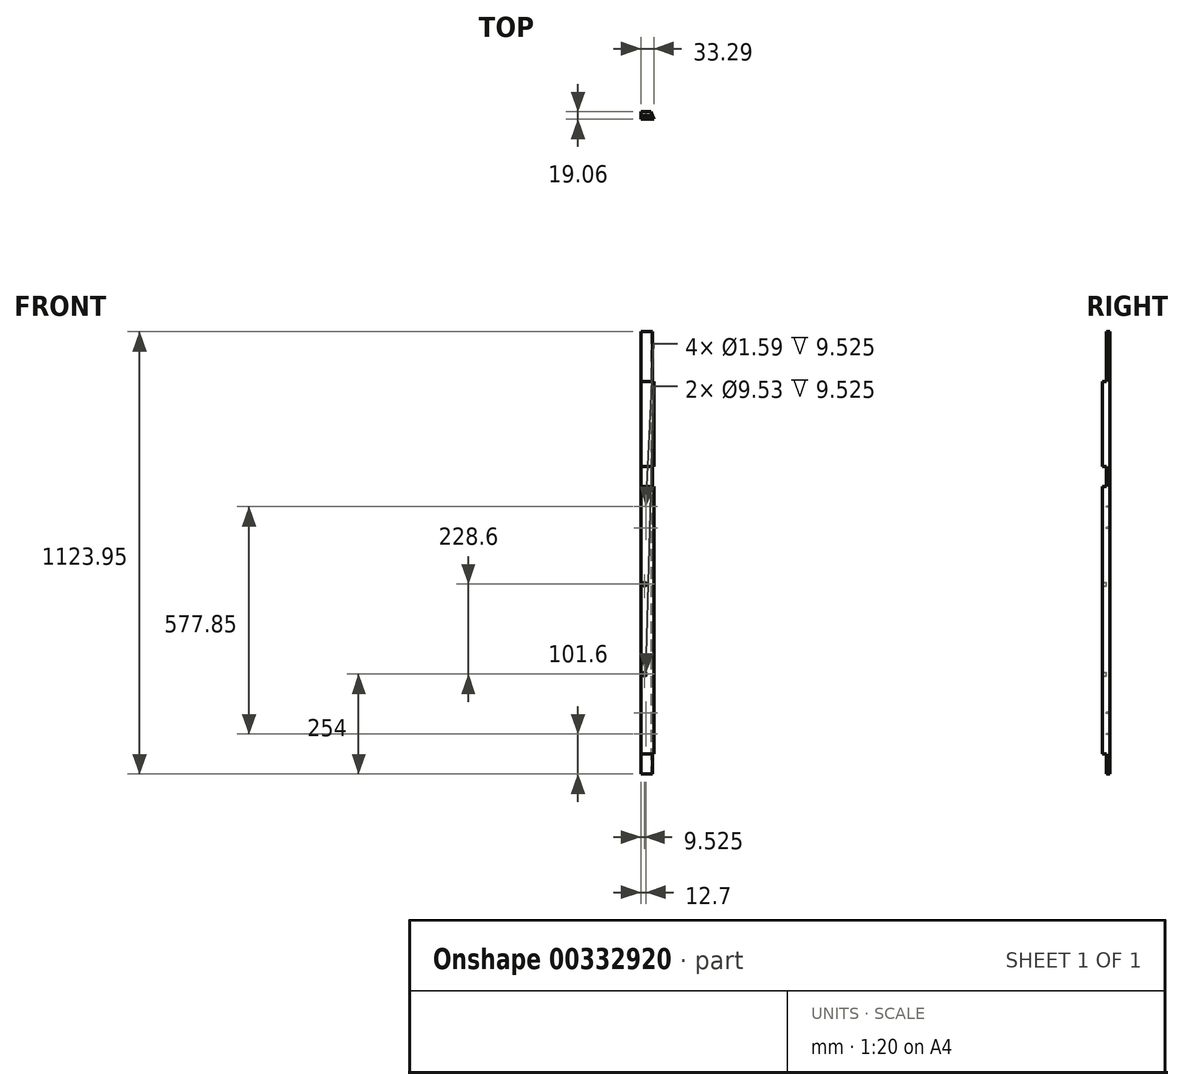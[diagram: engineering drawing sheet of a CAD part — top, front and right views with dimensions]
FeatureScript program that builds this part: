
annotation { "Feature Type Name" : "Feature", "Feature Type Description" : "" }
export const myFeature = defineFeature(function(context is Context, id is Id, definition is map)
    precondition{}
    {
        {
            var Q0;
            Q0=qCreatedBy(makeId("Top.planeOp"),FACE);
            var sketch = newSketch(context, id + "F0", { "sketchPlane" : qUnion([Q0])});
            skLineSegment(sketch, "E0.bottom", {"start": v(0, 9.53) * mm, "end": v(-25.4, 9.53) * mm});
            skLineSegment(sketch, "E0.top", {"start": v(7.9, -9.53) * mm, "end": v(-25.4, -9.53) * mm});
            skLineSegment(sketch, "E0.right", {"start": v(-25.4, 9.53) * mm, "end": v(-25.4, -9.53) * mm});
            skPoint(sketch, "E0.middle", {"position": v(0, 0) * mm});
            skLineSegment(sketch, "E1", {"start": v(0, 9.53) * mm, "end": v(7.9, -9.53) * mm});
            skPoint(sketch, "E0.left.end.orphan", {"position": v(25.4, -9.52) * mm});
            skPoint(sketch, "E2.orphan", {"position": v(25.4, 9.53) * mm});
            skSolve(sketch);
        }
        {
            var Q0;
            Q0=makeQuery(id+"F0.imprint","IMPRINT",FACE,{"disambiguationData":[TD([[makeQuery(id+"F0.imprint","IMPRINT",EDGE,{"derivedFrom":sQuery(id+"F0.wireOp",EDGE,"E0.bottom")}),1.0]])]});
            extrude(context, id + "F1", {"entities" : qUnion([Q0]), "depth" : 1123.95 * mm});
        }
        {
            var Q0;
            Q0=qCreatedBy(makeId("Front.planeOp"),FACE);
            var sketch = newSketch(context, id + "F2", { "sketchPlane" : qUnion([Q0])});
            skLineSegment(sketch, "E3.bottom", {"start": v(-38.77, 0) * mm, "end": v(83.66, 0) * mm});
            skLineSegment(sketch, "E3.top", {"start": v(-38.77, 50.8) * mm, "end": v(83.66, 50.8) * mm});
            skLineSegment(sketch, "E3.left", {"start": v(-38.77, 0) * mm, "end": v(-38.77, 50.8) * mm});
            skLineSegment(sketch, "E3.right", {"start": v(83.66, 0) * mm, "end": v(83.66, 50.8) * mm});
            skLineSegment(sketch, "E4.bottom", {"start": v(-44.21, 730.25) * mm, "end": v(49.65, 730.25) * mm});
            skLineSegment(sketch, "E4.top", {"start": v(-44.21, 781.05) * mm, "end": v(49.65, 781.05) * mm});
            skLineSegment(sketch, "E4.left", {"start": v(-44.21, 730.25) * mm, "end": v(-44.21, 781.05) * mm});
            skLineSegment(sketch, "E4.right", {"start": v(49.65, 730.25) * mm, "end": v(49.65, 781.05) * mm});
            skLineSegment(sketch, "E5.bottom", {"start": v(-210.36, 996.95) * mm, "end": v(132.8, 996.95) * mm});
            skLineSegment(sketch, "E5.top", {"start": v(-210.36, 1123.95) * mm, "end": v(132.8, 1123.95) * mm});
            skLineSegment(sketch, "E5.left", {"start": v(-210.36, 996.95) * mm, "end": v(-210.36, 1123.95) * mm});
            skLineSegment(sketch, "E5.right", {"start": v(132.8, 996.95) * mm, "end": v(132.8, 1123.95) * mm});
            skSolve(sketch);
        }
        {
            var Q0;
            Q0=qSketchRegion(id+"F2",true);
            extrude(context, id + "F3", {"entities" : qUnion([Q0]), "operationType" : NewBodyOperationType.REMOVE, "depth" : 25.4 * mm});
        }
        {
            var Q0;
            Q0=qCreatedBy(makeId("Front.planeOp"),FACE);
            var sketch = newSketch(context, id + "F4", { "sketchPlane" : qUnion([Q0])});
            skCircle(sketch, "E6", {"center": v(12.7, 101.6) * mm, "radius": 0.8 * mm});
            skCircle(sketch, "E7", {"center": v(12.7, 155.58) * mm, "radius": 0.8 * mm});
            skCircle(sketch, "E8", {"center": v(12.7, 625.48) * mm, "radius": 0.8 * mm});
            skCircle(sketch, "E9", {"center": v(12.7, 679.45) * mm, "radius": 0.8 * mm});
            skLineSegment(sketch, "E10", {"start": v(0, 0) * mm, "end": v(0, 1192.46) * mm, "construction": true});
            skLineSegment(sketch, "E11.bottom", {"start": v(12.7, 101.6) * mm, "end": v(-12.7, 101.6) * mm, "construction": true});
            skLineSegment(sketch, "E11.top", {"start": v(12.7, 679.45) * mm, "end": v(-12.7, 679.45) * mm, "construction": true});
            skLineSegment(sketch, "E11.left", {"start": v(12.7, 101.6) * mm, "end": v(12.7, 679.45) * mm, "construction": true});
            skLineSegment(sketch, "E11.right", {"start": v(-12.7, 101.6) * mm, "end": v(-12.7, 679.45) * mm, "construction": true});
            skCircle(sketch, "E12", {"center": v(-12.7, 625.48) * mm, "radius": 0.8 * mm});
            skCircle(sketch, "E13", {"center": v(-12.7, 679.45) * mm, "radius": 0.8 * mm});
            skCircle(sketch, "E14", {"center": v(-12.7, 101.6) * mm, "radius": 0.8 * mm});
            skCircle(sketch, "E15", {"center": v(-12.7, 155.58) * mm, "radius": 0.8 * mm});
            skSolve(sketch);
        }
        {
            var Q0;
            Q0=qSketchRegion(id+"F4",true);
            extrude(context, id + "F5", {"entities" : qUnion([Q0]), "operationType" : NewBodyOperationType.REMOVE, "oppositeDirection" : true, "depth" : 25.4 * mm});
        }
        {
            var Q0;
            Q0=qCreatedBy(makeId("Front.planeOp"),FACE);
            var sketch = newSketch(context, id + "F6", { "sketchPlane" : qUnion([Q0])});
            skCircle(sketch, "E16", {"center": v(-15.88, 254) * mm, "radius": 4.76 * mm});
            skCircle(sketch, "E17", {"center": v(-15.88, 482.6) * mm, "radius": 4.76 * mm});
            skSolve(sketch);
        }
        {
            var Q0;
            Q0 = qSketchRegion(id + "F6", true);
            extrude(context, id + "F7", {"entities" : qUnion([Q0]), "operationType" : NewBodyOperationType.REMOVE, "depth" : 25.4 * mm});
        }
    });
